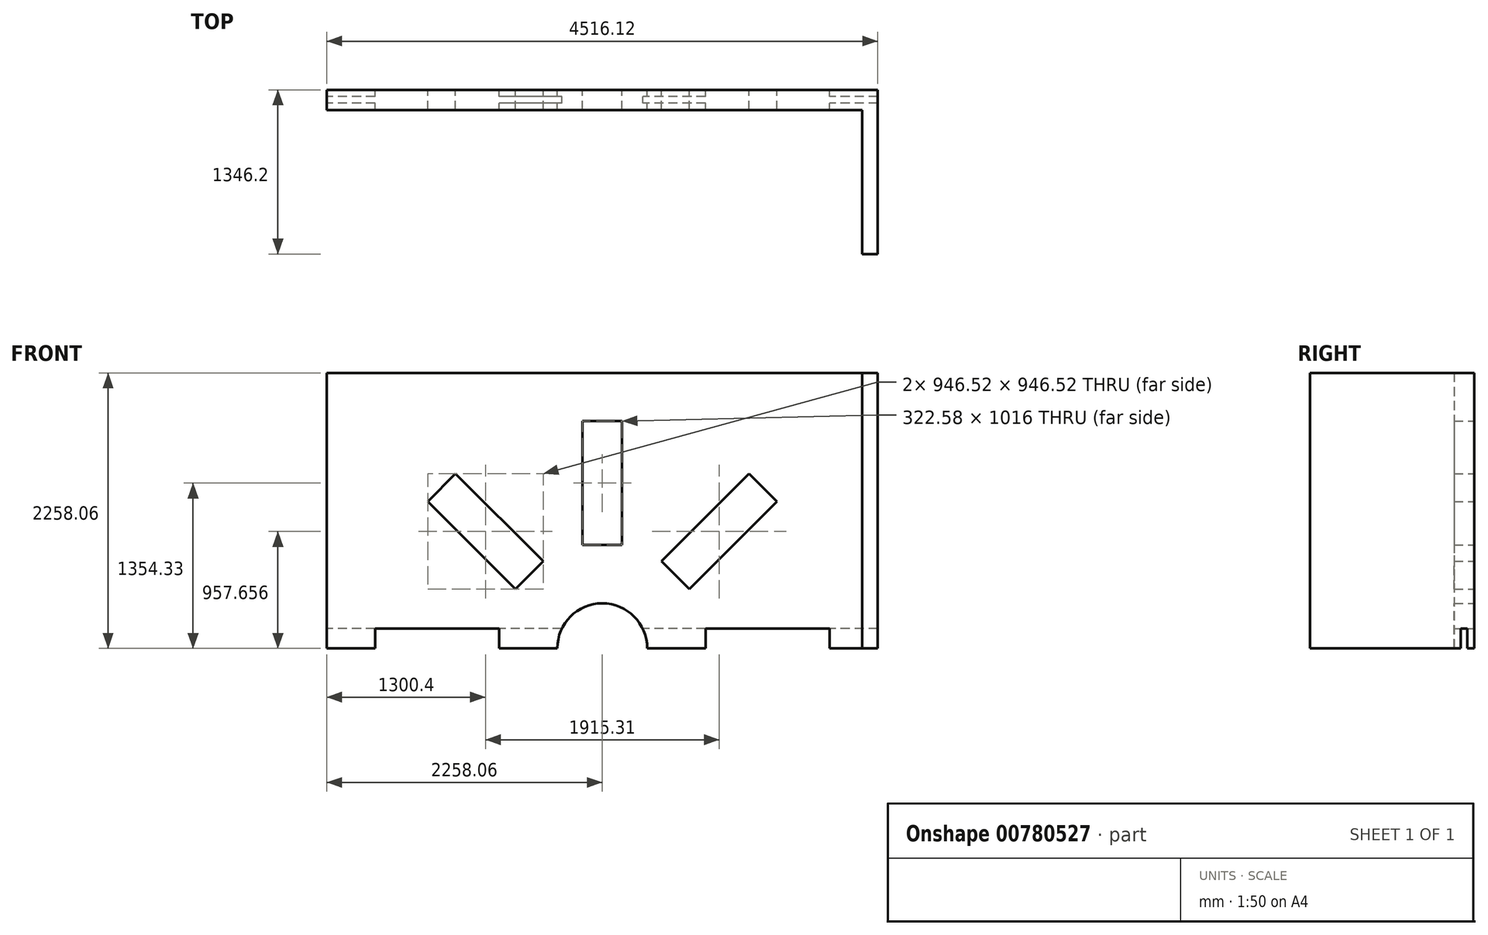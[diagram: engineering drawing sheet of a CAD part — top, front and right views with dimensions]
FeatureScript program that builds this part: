
annotation { "Feature Type Name" : "Feature", "Feature Type Description" : "" }
export const myFeature = defineFeature(function(context is Context, id is Id, definition is map)
    precondition{}
    {
        {
            var Q0;
            Q0=qCreatedBy(makeId("Front.planeOp"),FACE);
            var sketch = newSketch(context, id + "F0", { "sketchPlane" : qUnion([Q0])});
            skLineSegment(sketch, "E0.bottom", {"start": v(2258.06, 903.73) * mm, "end": v(-2258.06, 903.73) * mm});
            skLineSegment(sketch, "E0.top", {"start": v(2258.06, -1354.33) * mm, "end": v(-2258.06, -1354.33) * mm});
            skLineSegment(sketch, "E0.left", {"start": v(2258.06, 903.73) * mm, "end": v(2258.06, -1354.33) * mm});
            skLineSegment(sketch, "E0.right", {"start": v(-2258.06, 903.73) * mm, "end": v(-2258.06, -1354.33) * mm});
            skCircle(sketch, "E1", {"center": v(0, -1354.33) * mm, "radius": 368.3 * mm});
            skArc(sketch, "E2", {"start": v(-1935.48, -1354.33) * mm, "mid": v(0, 581.15) * mm, "end": v(1935.48, -1354.33) * mm});
            skLineSegment(sketch, "E3", {"start": v(0, -1354.33) * mm, "end": v(0, 581.15) * mm});
            skLineSegment(sketch, "E4.bottom", {"start": v(-161.29, 508) * mm, "end": v(161.3, 508) * mm});
            skLineSegment(sketch, "E4.top", {"start": v(-161.3, -508) * mm, "end": v(161.29, -508) * mm});
            skLineSegment(sketch, "E4.left", {"start": v(-161.29, 508) * mm, "end": v(-161.3, -508) * mm});
            skLineSegment(sketch, "E4.right", {"start": v(161.3, 508) * mm, "end": v(161.29, -508) * mm});
            skLineSegment(sketch, "E5.1.0", {"start": v(-1430.91, -151.51) * mm, "end": v(-712.5, -869.93) * mm});
            skLineSegment(sketch, "E5.1.1", {"start": v(-1430.91, -151.51) * mm, "end": v(-1202.82, 76.59) * mm});
            skLineSegment(sketch, "E5.1.2", {"start": v(-1202.82, 76.59) * mm, "end": v(-484.4, -641.83) * mm});
            skLineSegment(sketch, "E5.1.3", {"start": v(-712.5, -869.93) * mm, "end": v(-484.4, -641.83) * mm});
            skLineSegment(sketch, "E5.2.0", {"start": v(-1862.33, -1515.62) * mm, "end": v(-846.33, -1515.62) * mm});
            skLineSegment(sketch, "E5.2.1", {"start": v(-1862.33, -1515.62) * mm, "end": v(-1862.33, -1193.04) * mm});
            skLineSegment(sketch, "E5.2.2", {"start": v(-1862.33, -1193.04) * mm, "end": v(-846.33, -1193.04) * mm});
            skLineSegment(sketch, "E5.2.3", {"start": v(-846.33, -1515.62) * mm, "end": v(-846.33, -1193.04) * mm});
            skLineSegment(sketch, "E5.3.0", {"start": v(-1202.82, -2785.24) * mm, "end": v(-484.4, -2066.82) * mm});
            skLineSegment(sketch, "E5.3.1", {"start": v(-1202.82, -2785.24) * mm, "end": v(-1430.91, -2557.14) * mm});
            skLineSegment(sketch, "E5.3.2", {"start": v(-1430.91, -2557.14) * mm, "end": v(-712.5, -1838.72) * mm});
            skLineSegment(sketch, "E5.3.3", {"start": v(-484.4, -2066.82) * mm, "end": v(-712.5, -1838.72) * mm});
            skLineSegment(sketch, "E5.4.0", {"start": v(161.29, -3216.66) * mm, "end": v(161.29, -2200.66) * mm});
            skLineSegment(sketch, "E5.4.1", {"start": v(161.29, -3216.66) * mm, "end": v(-161.3, -3216.66) * mm});
            skLineSegment(sketch, "E5.4.2", {"start": v(-161.3, -3216.66) * mm, "end": v(-161.3, -2200.66) * mm});
            skLineSegment(sketch, "E5.4.3", {"start": v(161.29, -2200.66) * mm, "end": v(-161.3, -2200.66) * mm});
            skLineSegment(sketch, "E5.5.0", {"start": v(1430.91, -2557.14) * mm, "end": v(712.5, -1838.72) * mm});
            skLineSegment(sketch, "E5.5.1", {"start": v(1430.91, -2557.14) * mm, "end": v(1202.82, -2785.24) * mm});
            skLineSegment(sketch, "E5.5.2", {"start": v(1202.82, -2785.24) * mm, "end": v(484.4, -2066.82) * mm});
            skLineSegment(sketch, "E5.5.3", {"start": v(712.5, -1838.72) * mm, "end": v(484.4, -2066.82) * mm});
            skLineSegment(sketch, "E5.6.0", {"start": v(1862.33, -1193.04) * mm, "end": v(846.33, -1193.04) * mm});
            skLineSegment(sketch, "E5.6.1", {"start": v(1862.33, -1193.04) * mm, "end": v(1862.33, -1515.62) * mm});
            skLineSegment(sketch, "E5.6.2", {"start": v(1862.33, -1515.62) * mm, "end": v(846.33, -1515.62) * mm});
            skLineSegment(sketch, "E5.6.3", {"start": v(846.33, -1193.04) * mm, "end": v(846.33, -1515.62) * mm});
            skLineSegment(sketch, "E6.2.7.0", {"start": v(1202.82, 76.59) * mm, "end": v(484.4, -641.83) * mm});
            skLineSegment(sketch, "E6.3.7.0", {"start": v(1202.82, 76.59) * mm, "end": v(1430.91, -151.51) * mm});
            skLineSegment(sketch, "E6.6.7.0", {"start": v(1430.91, -151.51) * mm, "end": v(712.5, -869.93) * mm});
            skLineSegment(sketch, "E6.9.7.0", {"start": v(484.4, -641.83) * mm, "end": v(712.5, -869.93) * mm});
            skSolve(sketch);
        }
        {
            var Q0;
            Q0=makeQuery(id+"F0.imprint","IMPRINT",FACE,{"disambiguationData":[TD([[makeQuery(id+"F0.imprint","IMPRINT",EDGE,{"derivedFrom":sQuery(id+"F0.wireOp",EDGE,"E0.bottom")}),1.0]])]});
            var Q1;
            {var subQ0=sQuery(id+"F0.wireOp",EDGE,"E4.left");Q1=makeQuery(id+"F0.imprint","IMPRINT",FACE,{"disambiguationData":[TD([[makeQuery(id+"F0.imprint","IMPRINT",EDGE,{"derivedFrom":subQ0}),-1.0]])]});}
            var Q2;
            {var subQ0=sQuery(id+"F0.wireOp",EDGE,"E4.right");Q2=makeQuery(id+"F0.imprint","IMPRINT",FACE,{"disambiguationData":[TD([[makeQuery(id+"F0.imprint","IMPRINT",EDGE,{"derivedFrom":subQ0}),1.0]])]});}
            extrude(context, id + "F1", {"entities" : qUnion([Q0, Q1, Q2]), "endBound" : BoundingType.SYMMETRIC, "depth" : 165.1 * mm, "offsetDistance" : 25.4 * mm});
        }
        {
            var Q0;
            Q0=makeQuery(id+"F1.opExtrude","CAP_FACE",FACE,{"disambiguationData":[OSD([sQuery(id+"F0.wireOp",EDGE,"E0.bottom"),sQuery(id+"F0.wireOp",EDGE,"E0.top"),sQuery(id+"F0.wireOp",EDGE,"E0.left"),sQuery(id+"F0.wireOp",EDGE,"E0.right"),sQuery(id+"F0.wireOp",EDGE,"E1"),sQuery(id+"F0.wireOp",EDGE,"E4.bottom"),sQuery(id+"F0.wireOp",EDGE,"E4.top"),sQuery(id+"F0.wireOp",EDGE,"E4.left"),sQuery(id+"F0.wireOp",EDGE,"E4.right"),sQuery(id+"F0.wireOp",EDGE,"E5.1.0"),sQuery(id+"F0.wireOp",EDGE,"E5.1.1"),sQuery(id+"F0.wireOp",EDGE,"E5.1.2"),sQuery(id+"F0.wireOp",EDGE,"E5.1.3"),sQuery(id+"F0.wireOp",EDGE,"E5.2.1"),sQuery(id+"F0.wireOp",EDGE,"E5.2.2"),sQuery(id+"F0.wireOp",EDGE,"E5.2.3"),sQuery(id+"F0.wireOp",EDGE,"E5.6.0"),sQuery(id+"F0.wireOp",EDGE,"E5.6.1"),sQuery(id+"F0.wireOp",EDGE,"E5.6.3"),sQuery(id+"F0.wireOp",EDGE,"E6.2.7.0"),sQuery(id+"F0.wireOp",EDGE,"E6.3.7.0"),sQuery(id+"F0.wireOp",EDGE,"E6.6.7.0"),sQuery(id+"F0.wireOp",EDGE,"E6.9.7.0")])],"isStart":false});
            var sketch = newSketch(context, id + "F2", { "sketchPlane" : qUnion([Q0])});
            skLineSegment(sketch, "E7.bottom", {"start": v(2258.06, 903.73) * mm, "end": v(2131.06, 903.73) * mm});
            skLineSegment(sketch, "E7.top", {"start": v(2258.06, -1354.33) * mm, "end": v(2131.06, -1354.33) * mm});
            skLineSegment(sketch, "E7.left", {"start": v(2258.06, 903.73) * mm, "end": v(2258.06, -1354.33) * mm});
            skLineSegment(sketch, "E7.right", {"start": v(2131.06, 903.73) * mm, "end": v(2131.06, -1354.33) * mm});
            skSolve(sketch);
        }
        {
            var Q0;
            Q0 = qSketchRegion(id + "F2", true);
            extrude(context, id + "F3", {"entities" : qUnion([Q0]), "operationType" : NewBodyOperationType.ADD, "depth" : 1181.1 * mm, "offsetDistance" : 25.4 * mm});
        }
        {
            var Q0;
            Q0=makeQuery(id+"F1.opExtrude","SWEPT_FACE",FACE,{"disambiguationData":[OSD([sQuery(id+"F0.wireOp",EDGE,"E0.right")])]});
            var sketch = newSketch(context, id + "F4", { "sketchPlane" : qUnion([Q0])});
            skLineSegment(sketch, "E8.bottom", {"start": v(-27.52, -1354.33) * mm, "end": v(27.52, -1354.33) * mm});
            skLineSegment(sketch, "E8.top", {"start": v(-27.52, -1193.04) * mm, "end": v(27.52, -1193.04) * mm});
            skLineSegment(sketch, "E8.left", {"start": v(-27.52, -1354.33) * mm, "end": v(-27.52, -1193.04) * mm});
            skLineSegment(sketch, "E8.right", {"start": v(27.52, -1354.33) * mm, "end": v(27.52, -1193.04) * mm});
            skLineSegment(sketch, "E9.bottom", {"start": v(-82.55, -1354.33) * mm, "end": v(-27.52, -1354.33) * mm});
            skLineSegment(sketch, "E9.top", {"start": v(-82.55, -1354.33) * mm, "end": v(-27.52, -1354.33) * mm});
            skLineSegment(sketch, "E9.left", {"start": v(-82.55, -1354.33) * mm, "end": v(-82.55, -1354.33) * mm});
            skLineSegment(sketch, "E9.right", {"start": v(-27.52, -1354.33) * mm, "end": v(-27.52, -1354.33) * mm});
            skSolve(sketch);
        }
        {
            var Q0;
            Q0=makeQuery(id+"F4.imprint","IMPRINT",FACE,{"disambiguationData":[TD([[makeQuery(id+"F4.imprint","IMPRINT",EDGE,{"derivedFrom":sQuery(id+"F4.wireOp",EDGE,"E8.bottom")}),-1.0]])]});
            extrude(context, id + "F5", {"entities" : qUnion([Q0]), "operationType" : NewBodyOperationType.REMOVE, "oppositeDirection" : true, "depth" : 4516.12 * mm, "offsetDistance" : 25.4 * mm});
        }
    });
